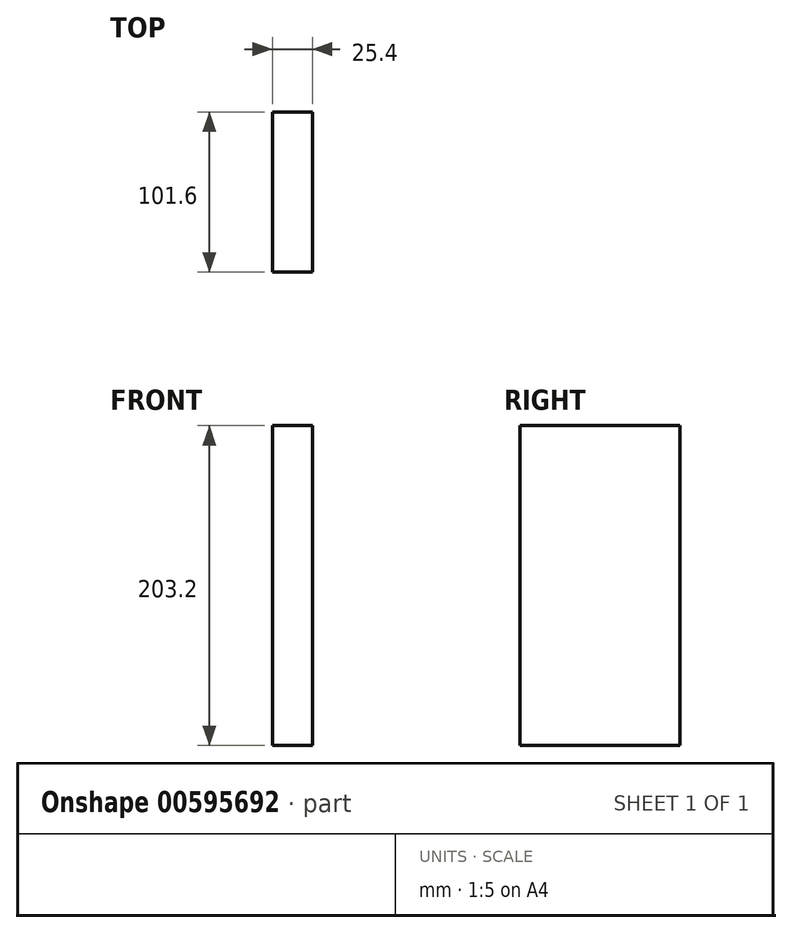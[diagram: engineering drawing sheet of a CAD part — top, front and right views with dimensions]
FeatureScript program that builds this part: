
annotation { "Feature Type Name" : "Feature", "Feature Type Description" : "" }
export const myFeature = defineFeature(function(context is Context, id is Id, definition is map)
    precondition{}
    {
        {
            var Q0;
            Q0=qCreatedBy(makeId("Top.planeOp"),FACE);
            var sketch = newSketch(context, id + "F0", { "sketchPlane" : qUnion([Q0])});
            skLineSegment(sketch, "E0.bottom", {"start": v(0, 0) * mm, "end": v(25.4, 0) * mm});
            skLineSegment(sketch, "E0.top", {"start": v(0, 101.6) * mm, "end": v(25.4, 101.6) * mm});
            skLineSegment(sketch, "E0.left", {"start": v(0, 0) * mm, "end": v(0, 101.6) * mm});
            skLineSegment(sketch, "E0.right", {"start": v(25.4, 0) * mm, "end": v(25.4, 101.6) * mm});
            skSolve(sketch);
        }
        {
            var Q0;
            Q0=makeQuery(id+"F0.imprint","IMPRINT",FACE,{"disambiguationData":[TD([[makeQuery(id+"F0.imprint","IMPRINT",EDGE,{"derivedFrom":sQuery(id+"F0.wireOp",EDGE,"E0.bottom")}),1.0]])]});
            extrude(context, id + "F1", {"entities" : qUnion([Q0]), "depth" : 203.2 * mm, "offsetDistance" : 25.4 * mm});
        }
    });
